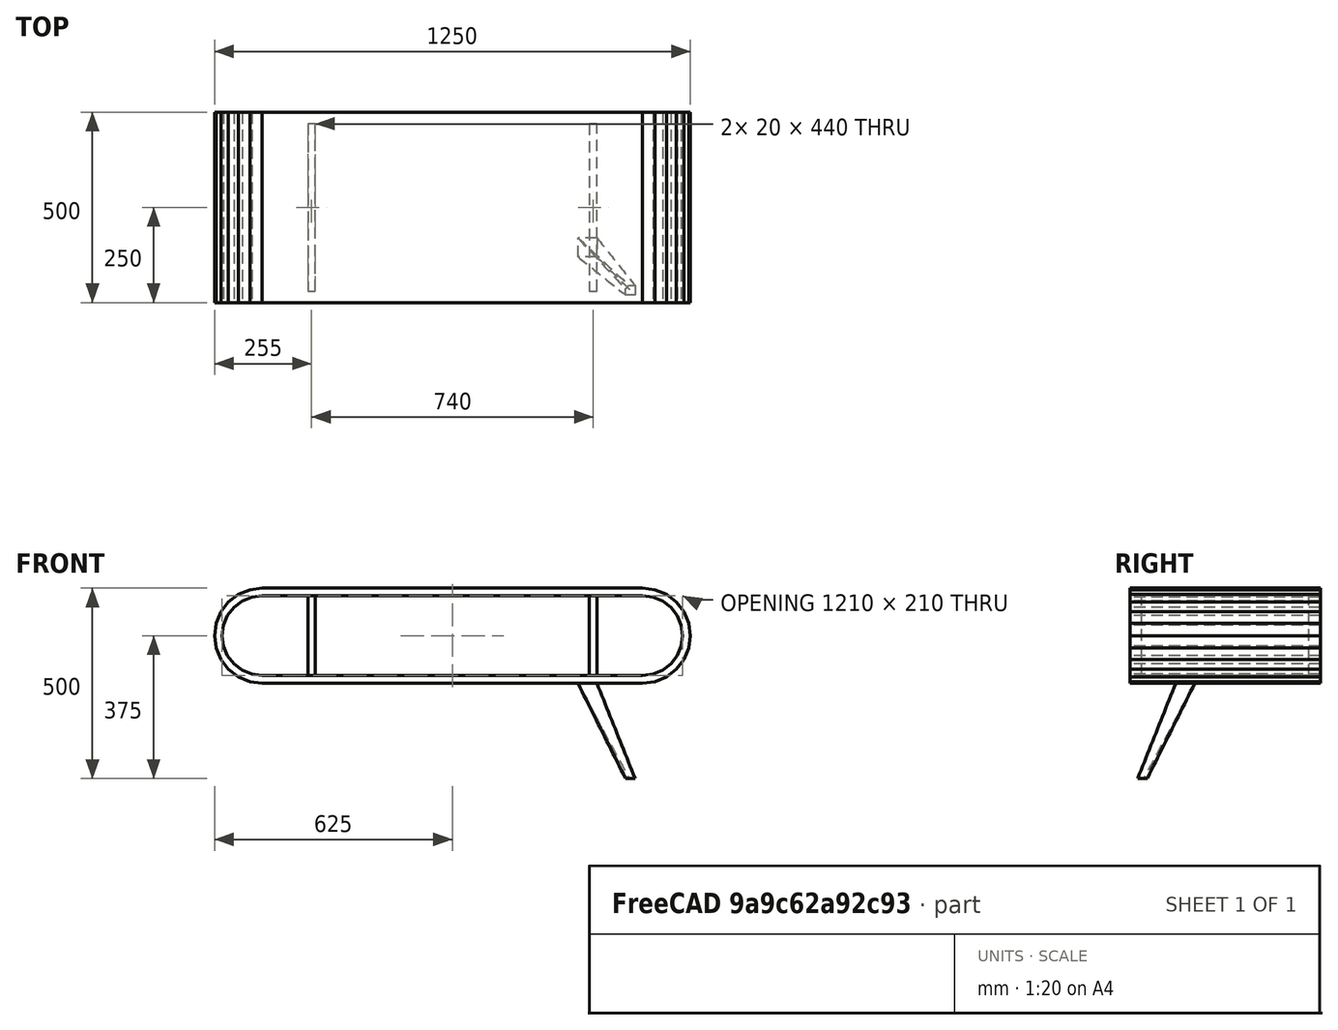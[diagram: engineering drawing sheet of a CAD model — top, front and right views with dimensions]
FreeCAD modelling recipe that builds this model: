
FCSTD DOCUMENT  (FreeCAD 0.22R35735 (Git))
Label: bendy
License: All rights reserved
LicenseURL: http://en.wikipedia.org/wiki/All_rights_reserved
objects: TechDraw::DrawViewDimension×14, Sketcher::SketchObject×4, PartDesign::Plane×4, Part::Mirroring×3, PartDesign::Pad×2, PartDesign::Body×2, TechDraw::DrawProjGroupItem×2, Spreadsheet::Sheet×1, PartDesign::AdditiveLoft×1, TechDraw::DrawSVGTemplate×1, TechDraw::DrawProjGroup×1, TechDraw::DrawPage×1
note: 41 computed .brp shape members not serialized (recipe doc carries the construction recipe); baked Part::Feature solids carry a one-line shape summary decoded from their .brp

FEATURE [Sketcher::SketchObject] Sketch
  FullyConstrained = true
  MapMode = 5
  Placement = pos=(0,0,0) rot=(1,0,0;1.5708rad)
  Support = -> [XZ_Plane]
  expr: Constraints[162] = Spreadsheet.thickness
  expr: Constraints[163] = Spreadsheet.thickness
  expr: Constraints[237] = Spreadsheet.total_height
  expr: Constraints[76] = Spreadsheet.total_length
  expr: Constraints[80] = Spreadsheet.top_height
  sketch-geometry (106):
    g0: LineSegment StartX=-4.97e-14 StartY=500 StartZ=0 EndX=1000 EndY=500 EndZ=0
    g1: LineSegment StartX=0 StartY=250 StartZ=0 EndX=1000 EndY=250 EndZ=0
    g2: LineSegment StartX=0 StartY=480 StartZ=0 EndX=1000 EndY=480 EndZ=0
    g3: LineSegment StartX=0 StartY=270 StartZ=0 EndX=1000 EndY=270 EndZ=0
    g4: LineSegment StartX=1105 StartY=375 StartZ=0 EndX=1101.42 EndY=402.176 EndZ=0
    g5: LineSegment StartX=1101.42 StartY=402.176 StartZ=0 EndX=1090.93 EndY=427.5 EndZ=0
    g6: LineSegment StartX=1090.93 StartY=427.5 StartZ=0 EndX=1074.25 EndY=449.246 EndZ=0
    g7: LineSegment StartX=1074.25 StartY=449.246 StartZ=0 EndX=1052.5 EndY=465.933 EndZ=0
    g8: LineSegment StartX=1052.5 StartY=465.933 StartZ=0 EndX=1027.18 EndY=476.422 EndZ=0
    g9: LineSegment StartX=1027.18 StartY=476.422 StartZ=0 EndX=1000 EndY=480 EndZ=0
    g10: LineSegment StartX=1000 StartY=480 StartZ=0 EndX=972.824 EndY=476.422 EndZ=0
    g11: LineSegment StartX=972.824 StartY=476.422 StartZ=0 EndX=947.5 EndY=465.933 EndZ=0
    g12: LineSegment StartX=947.5 StartY=465.933 StartZ=0 EndX=925.754 EndY=449.246 EndZ=0
    g13: LineSegment StartX=925.754 StartY=449.246 StartZ=0 EndX=909.067 EndY=427.5 EndZ=0
    g14: LineSegment StartX=909.067 StartY=427.5 StartZ=0 EndX=898.578 EndY=402.176 EndZ=0
    g15: LineSegment StartX=898.578 StartY=402.176 StartZ=0 EndX=895 EndY=375 EndZ=0
    g16: LineSegment StartX=895 StartY=375 StartZ=0 EndX=898.578 EndY=347.824 EndZ=0
    g17: LineSegment StartX=898.578 StartY=347.824 StartZ=0 EndX=909.067 EndY=322.5 EndZ=0
    g18: LineSegment StartX=909.067 StartY=322.5 StartZ=0 EndX=925.754 EndY=300.754 EndZ=0
    g19: LineSegment StartX=925.754 StartY=300.754 StartZ=0 EndX=947.5 EndY=284.067 EndZ=0
    g20: LineSegment StartX=947.5 StartY=284.067 StartZ=0 EndX=972.824 EndY=273.578 EndZ=0
    g21: LineSegment StartX=972.824 StartY=273.578 StartZ=0 EndX=1000 EndY=270 EndZ=0
    g22: LineSegment StartX=1000 StartY=270 StartZ=0 EndX=1027.18 EndY=273.578 EndZ=0
    g23: LineSegment StartX=1027.18 StartY=273.578 StartZ=0 EndX=1052.5 EndY=284.067 EndZ=0
    g24: LineSegment StartX=1052.5 StartY=284.067 StartZ=0 EndX=1074.25 EndY=300.754 EndZ=0
    g25: LineSegment StartX=1074.25 StartY=300.754 StartZ=0 EndX=1090.93 EndY=322.5 EndZ=0
    g26: LineSegment StartX=1090.93 StartY=322.5 StartZ=0 EndX=1101.42 EndY=347.824 EndZ=0
    g27: LineSegment StartX=1101.42 StartY=347.824 StartZ=0 EndX=1105 EndY=375 EndZ=0
    g28: Circle CenterX=1000 CenterY=375 CenterZ=0 NormalX=0 NormalY=0 NormalZ=1 AngleXU=0 Radius=105
    g29: LineSegment StartX=0 StartY=480 StartZ=0 EndX=-27.176 EndY=476.422 EndZ=0
    g30: LineSegment StartX=-27.176 StartY=476.422 StartZ=0 EndX=-52.5 EndY=465.933 EndZ=0
    g31: LineSegment StartX=-52.5 StartY=465.933 StartZ=0 EndX=-74.2462 EndY=449.246 EndZ=0
    g32: LineSegment StartX=-74.2462 StartY=449.246 StartZ=0 EndX=-90.9327 EndY=427.5 EndZ=0
    g33: LineSegment StartX=-90.9327 StartY=427.5 StartZ=0 EndX=-101.422 EndY=402.176 EndZ=0
    g34: LineSegment StartX=-101.422 StartY=402.176 StartZ=0 EndX=-105 EndY=375 EndZ=0
    g35: LineSegment StartX=-105 StartY=375 StartZ=0 EndX=-101.422 EndY=347.824 EndZ=0
    g36: LineSegment StartX=-101.422 StartY=347.824 StartZ=0 EndX=-90.9327 EndY=322.5 EndZ=0
    g37: LineSegment StartX=-90.9327 StartY=322.5 StartZ=0 EndX=-74.2462 EndY=300.754 EndZ=0
    g38: LineSegment StartX=-74.2462 StartY=300.754 StartZ=0 EndX=-52.5 EndY=284.067 EndZ=0
    g39: LineSegment StartX=-52.5 StartY=284.067 StartZ=0 EndX=-27.176 EndY=273.578 EndZ=0
    g40: LineSegment StartX=-27.176 StartY=273.578 StartZ=0 EndX=-7.1e-15 EndY=270 EndZ=0
    g41: LineSegment StartX=-7.1e-15 StartY=270 StartZ=0 EndX=27.176 EndY=273.578 EndZ=0
    g42: LineSegment StartX=27.176 StartY=273.578 StartZ=0 EndX=52.5 EndY=284.067 EndZ=0
    g43: LineSegment StartX=52.5 StartY=284.067 StartZ=0 EndX=74.2462 EndY=300.754 EndZ=0
    g44: LineSegment StartX=74.2462 StartY=300.754 StartZ=0 EndX=90.9327 EndY=322.5 EndZ=0
    g45: LineSegment StartX=90.9327 StartY=322.5 StartZ=0 EndX=101.422 EndY=347.824 EndZ=0
    g46: LineSegment StartX=101.422 StartY=347.824 StartZ=0 EndX=105 EndY=375 EndZ=0
    g47: LineSegment StartX=105 StartY=375 StartZ=0 EndX=101.422 EndY=402.176 EndZ=0
    g48: LineSegment StartX=101.422 StartY=402.176 StartZ=0 EndX=90.9327 EndY=427.5 EndZ=0
    g49: LineSegment StartX=90.9327 StartY=427.5 StartZ=0 EndX=74.2462 EndY=449.246 EndZ=0
    g50: LineSegment StartX=74.2462 StartY=449.246 StartZ=0 EndX=52.5 EndY=465.933 EndZ=0
    g51: LineSegment StartX=52.5 StartY=465.933 StartZ=0 EndX=27.176 EndY=476.422 EndZ=0
    g52: LineSegment StartX=27.176 StartY=476.422 StartZ=0 EndX=0 EndY=480 EndZ=0
    g53: Circle CenterX=0 CenterY=375 CenterZ=0 NormalX=0 NormalY=0 NormalZ=1 AngleXU=0 Radius=105
    g54: LineSegment StartX=0 StartY=480 StartZ=0 EndX=0 EndY=375 EndZ=0
    g55: LineSegment StartX=0 StartY=375 StartZ=0 EndX=0 EndY=270 EndZ=0
    g56: LineSegment StartX=-4.97e-14 StartY=500 StartZ=0 EndX=-32.3524 EndY=495.741 EndZ=0
    g57: LineSegment StartX=-32.3524 StartY=495.741 StartZ=0 EndX=-62.5 EndY=483.253 EndZ=0
    g58: LineSegment StartX=-62.5 StartY=483.253 StartZ=0 EndX=-88.3883 EndY=463.388 EndZ=0
    g59: LineSegment StartX=-88.3883 StartY=463.388 StartZ=0 EndX=-108.253 EndY=437.5 EndZ=0
    g60: LineSegment StartX=-108.253 StartY=437.5 StartZ=0 EndX=-120.741 EndY=407.352 EndZ=0
    g61: LineSegment StartX=-120.741 StartY=407.352 StartZ=0 EndX=-125 EndY=375 EndZ=0
    g62: LineSegment StartX=-125 StartY=375 StartZ=0 EndX=-120.741 EndY=342.648 EndZ=0
    g63: LineSegment StartX=-120.741 StartY=342.648 StartZ=0 EndX=-108.253 EndY=312.5 EndZ=0
    g64: LineSegment StartX=-108.253 StartY=312.5 StartZ=0 EndX=-88.3883 EndY=286.612 EndZ=0
    g65: LineSegment StartX=-88.3883 StartY=286.612 StartZ=0 EndX=-62.5 EndY=266.747 EndZ=0
    g66: LineSegment StartX=-62.5 StartY=266.747 StartZ=0 EndX=-32.3524 EndY=254.259 EndZ=0
    g67: LineSegment StartX=-32.3524 StartY=254.259 StartZ=0 EndX=4.97e-14 EndY=250 EndZ=0
    g68: LineSegment StartX=4.97e-14 StartY=250 StartZ=0 EndX=32.3524 EndY=254.259 EndZ=0
    g69: LineSegment StartX=32.3524 StartY=254.259 StartZ=0 EndX=62.5 EndY=266.747 EndZ=0
    g70: LineSegment StartX=62.5 StartY=266.747 StartZ=0 EndX=88.3883 EndY=286.612 EndZ=0
    g71: LineSegment StartX=88.3883 StartY=286.612 StartZ=0 EndX=108.253 EndY=312.5 EndZ=0
    g72: LineSegment StartX=108.253 StartY=312.5 StartZ=0 EndX=120.741 EndY=342.648 EndZ=0
    g73: LineSegment StartX=120.741 StartY=342.648 StartZ=0 EndX=125 EndY=375 EndZ=0
    g74: LineSegment StartX=125 StartY=375 StartZ=0 EndX=120.741 EndY=407.352 EndZ=0
    g75: LineSegment StartX=120.741 StartY=407.352 StartZ=0 EndX=108.253 EndY=437.5 EndZ=0
    g76: LineSegment StartX=108.253 StartY=437.5 StartZ=0 EndX=88.3883 EndY=463.388 EndZ=0
    g77: LineSegment StartX=88.3883 StartY=463.388 StartZ=0 EndX=62.5 EndY=483.253 EndZ=0
    g78: LineSegment StartX=62.5 StartY=483.253 StartZ=0 EndX=32.3524 EndY=495.741 EndZ=0
    g79: LineSegment StartX=32.3524 StartY=495.741 StartZ=0 EndX=-4.97e-14 EndY=500 EndZ=0
    g80: Circle CenterX=0 CenterY=375 CenterZ=0 NormalX=0 NormalY=0 NormalZ=1 AngleXU=0 Radius=125
    g81: LineSegment StartX=1000 StartY=500 StartZ=0 EndX=967.648 EndY=495.741 EndZ=0
    g82: LineSegment StartX=967.648 StartY=495.741 StartZ=0 EndX=937.5 EndY=483.253 EndZ=0
    g83: LineSegment StartX=937.5 StartY=483.253 StartZ=0 EndX=911.612 EndY=463.388 EndZ=0
    g84: LineSegment StartX=911.612 StartY=463.388 StartZ=0 EndX=891.747 EndY=437.5 EndZ=0
    g85: LineSegment StartX=891.747 StartY=437.5 StartZ=0 EndX=879.259 EndY=407.352 EndZ=0
    g86: LineSegment StartX=879.259 StartY=407.352 StartZ=0 EndX=875 EndY=375 EndZ=0
    g87: LineSegment StartX=875 StartY=375 StartZ=0 EndX=879.259 EndY=342.648 EndZ=0
    g88: LineSegment StartX=879.259 StartY=342.648 StartZ=0 EndX=891.747 EndY=312.5 EndZ=0
    g89: LineSegment StartX=891.747 StartY=312.5 StartZ=0 EndX=911.612 EndY=286.612 EndZ=0
    g90: LineSegment StartX=911.612 StartY=286.612 StartZ=0 EndX=937.5 EndY=266.747 EndZ=0
    g91: LineSegment StartX=937.5 StartY=266.747 StartZ=0 EndX=967.648 EndY=254.259 EndZ=0
    g92: LineSegment StartX=967.648 StartY=254.259 StartZ=0 EndX=1000 EndY=250 EndZ=0
    g93: LineSegment StartX=1000 StartY=250 StartZ=0 EndX=1032.35 EndY=254.259 EndZ=0
    g94: LineSegment StartX=1032.35 StartY=254.259 StartZ=0 EndX=1062.5 EndY=266.747 EndZ=0
    g95: LineSegment StartX=1062.5 StartY=266.747 StartZ=0 EndX=1088.39 EndY=286.612 EndZ=0
    g96: LineSegment StartX=1088.39 StartY=286.612 StartZ=0 EndX=1108.25 EndY=312.5 EndZ=0
    g97: LineSegment StartX=1108.25 StartY=312.5 StartZ=0 EndX=1120.74 EndY=342.648 EndZ=0
    g98: LineSegment StartX=1120.74 StartY=342.648 StartZ=0 EndX=1125 EndY=375 EndZ=0
    g99: LineSegment StartX=1125 StartY=375 StartZ=0 EndX=1120.74 EndY=407.352 EndZ=0
    g100: LineSegment StartX=1120.74 StartY=407.352 StartZ=0 EndX=1108.25 EndY=437.5 EndZ=0
    g101: LineSegment StartX=1108.25 StartY=437.5 StartZ=0 EndX=1088.39 EndY=463.388 EndZ=0
    g102: LineSegment StartX=1088.39 StartY=463.388 StartZ=0 EndX=1062.5 EndY=483.253 EndZ=0
    g103: LineSegment StartX=1062.5 StartY=483.253 StartZ=0 EndX=1032.35 EndY=495.741 EndZ=0
    g104: LineSegment StartX=1032.35 StartY=495.741 StartZ=0 EndX=1000 EndY=500 EndZ=0
    g105: Circle CenterX=1000 CenterY=375 CenterZ=0 NormalX=0 NormalY=0 NormalZ=1 AngleXU=0 Radius=125
  constraints (226):
    c: Horizontal(g0)
    c: Horizontal(g2)
    c: Coincident(g4,g5)
    c: Coincident(g5,g6)
    c: Coincident(g6,g7)
    c: Coincident(g7,g8)
    c: Coincident(g8,g9)
    c: Coincident(g9,g10)
    c: Coincident(g10,g11)
    c: Coincident(g11,g12)
    c: Coincident(g12,g13)
    c: Coincident(g13,g14)
    c: Coincident(g14,g15)
    c: Coincident(g15,g16)
    c: Coincident(g16,g17)
    c: Coincident(g17,g18)
    c: Coincident(g18,g19)
    c: Coincident(g19,g20)
    c: Coincident(g20,g21)
    c: Coincident(g21,g22)
    c: Coincident(g22,g23)
    c: Coincident(g23,g24)
    c: Coincident(g24,g25)
    c: Coincident(g25,g26)
    c: Coincident(g26,g27)
    c: Coincident(g27,g4)
    c: Equal(g4, g5-g27) x23
    c: PointOnObject(g4,g28)
    c: PointOnObject(g5,g28)
    c: PointOnObject(g6,g28)
    c: PointOnObject(g7,g28)
    c: PointOnObject(g8,g28)
    c: PointOnObject(g9,g28)
    c: PointOnObject(g10,g28)
    c: PointOnObject(g11,g28)
    c: PointOnObject(g12,g28)
    c: PointOnObject(g13,g28)
    c: PointOnObject(g14,g28)
    c: PointOnObject(g15,g28)
    c: PointOnObject(g16,g28)
    c: PointOnObject(g17,g28)
    c: PointOnObject(g18,g28)
    c: PointOnObject(g19,g28)
    c: PointOnObject(g20,g28)
    c: PointOnObject(g21,g28)
    c: PointOnObject(g22,g28)
    c: PointOnObject(g23,g28)
    c: PointOnObject(g24,g28)
    c: PointOnObject(g25,g28)
    c: PointOnObject(g26,g28)
    c: PointOnObject(g27,g28)
    c: Equal(g0,g2)
    c: Equal(g2,g3)
    c: Equal(g3,g1)
    c: DistanceX(g0,g0) = 1000
    c: Vertical(g28,g2)
    c: Horizontal(g1)
    c: Horizontal(g3)
    c: DistanceY(g1,g0) = 250
    c: Coincident(g9,g2)
    c: Coincident(g29,g30)
    c: Coincident(g30,g31)
    c: Coincident(g31,g32)
    c: Coincident(g32,g33)
    c: Coincident(g33,g34)
    c: Coincident(g34,g35)
    c: Coincident(g35,g36)
    c: Coincident(g36,g37)
    c: Coincident(g37,g38)
    c: Coincident(g38,g39)
    c: Coincident(g39,g40)
    c: Coincident(g40,g41)
    c: Coincident(g41,g42)
    c: Coincident(g42,g43)
    c: Coincident(g43,g44)
    c: Coincident(g44,g45)
    c: Coincident(g45,g46)
    c: Coincident(g46,g47)
    c: Coincident(g47,g48)
    c: Coincident(g48,g49)
    c: Coincident(g49,g50)
    c: Coincident(g50,g51)
    c: Coincident(g51,g52)
    c: Coincident(g52,g29)
    c: Equal(g29, g30-g52) x23
    c: PointOnObject(g29,g53)
    c: PointOnObject(g30,g53)
    c: PointOnObject(g31,g53)
    c: PointOnObject(g32,g53)
    c: PointOnObject(g33,g53)
    c: PointOnObject(g34,g53)
    c: PointOnObject(g35,g53)
    c: PointOnObject(g36,g53)
    c: PointOnObject(g37,g53)
    c: PointOnObject(g38,g53)
    c: PointOnObject(g39,g53)
    c: PointOnObject(g40,g53)
    c: PointOnObject(g41,g53)
    c: PointOnObject(g42,g53)
    c: PointOnObject(g43,g53)
    c: PointOnObject(g44,g53)
    c: PointOnObject(g45,g53)
    c: PointOnObject(g46,g53)
    c: PointOnObject(g47,g53)
    c: PointOnObject(g48,g53)
    c: PointOnObject(g49,g53)
    c: PointOnObject(g50,g53)
    c: PointOnObject(g51,g53)
    c: PointOnObject(g52,g53)
    c: PointOnObject(g53,g-2)
    c: Coincident(g52,g2)
    c: Coincident(g54,g2)
    c: Coincident(g54,g53)
    c: Vertical(g54)
    c: Coincident(g55,g53)
    c: Coincident(g55,g3)
    c: Vertical(g55)
    c: Equal(g54,g55)
    c: DistanceY(g1,g3) = 20
    c: DistanceY(g2,g0) = 20
    c: Coincident(g56,g57)
    c: Coincident(g57,g58)
    c: Coincident(g58,g59)
    c: Coincident(g59,g60)
    c: Coincident(g60,g61)
    c: Coincident(g61,g62)
    c: Coincident(g62,g63)
    c: Coincident(g63,g64)
    c: Coincident(g64,g65)
    c: Coincident(g65,g66)
    c: Coincident(g66,g67)
    c: Coincident(g67,g68)
    c: Coincident(g68,g69)
    c: Coincident(g69,g70)
    c: Coincident(g70,g71)
    c: Coincident(g71,g72)
    c: Coincident(g72,g73)
    c: Coincident(g73,g74)
    c: Coincident(g74,g75)
    c: Coincident(g75,g76)
    c: Coincident(g76,g77)
    c: Coincident(g77,g78)
    c: Coincident(g78,g79)
    c: Coincident(g79,g56)
    c: Equal(g56, g57-g79) x23
    c: PointOnObject(g56,g80)
    c: PointOnObject(g57,g80)
    c: PointOnObject(g58,g80)
    c: PointOnObject(g59,g80)
    c: PointOnObject(g60,g80)
    c: PointOnObject(g61,g80)
    c: PointOnObject(g62,g80)
    c: PointOnObject(g63,g80)
    c: PointOnObject(g64,g80)
    c: PointOnObject(g65,g80)
    c: PointOnObject(g66,g80)
    c: PointOnObject(g67,g80)
    c: PointOnObject(g68,g80)
    c: PointOnObject(g69,g80)
    c: PointOnObject(g70,g80)
    c: PointOnObject(g71,g80)
    c: PointOnObject(g72,g80)
    c: PointOnObject(g73,g80)
    c: PointOnObject(g74,g80)
    c: PointOnObject(g75,g80)
    c: PointOnObject(g76,g80)
    c: PointOnObject(g77,g80)
    c: PointOnObject(g78,g80)
    c: PointOnObject(g79,g80)
    c: Horizontal(g28,g53)
    c: Coincident(g80,g53)
    c: DistanceY(g-1,g0) = 500
    c: Coincident(g0,g56)
    c: Vertical(g3,g1)
    c: Coincident(g81,g82)
    c: Coincident(g82,g83)
    c: Coincident(g83,g84)
    c: Coincident(g84,g85)
    c: Coincident(g85,g86)
    c: Coincident(g86,g87)
    c: Coincident(g87,g88)
    c: Coincident(g88,g89)
    c: Coincident(g89,g90)
    c: Coincident(g90,g91)
    c: Coincident(g91,g92)
    c: Coincident(g92,g93)
    c: Coincident(g93,g94)
    c: Coincident(g94,g95)
    c: Coincident(g95,g96)
    c: Coincident(g96,g97)
    c: Coincident(g97,g98)
    c: Coincident(g98,g99)
    c: Coincident(g99,g100)
    c: Coincident(g100,g101)
    c: Coincident(g101,g102)
    c: Coincident(g102,g103)
    c: Coincident(g103,g104)
    c: Coincident(g104,g81)
    c: Equal(g81, g82-g104) x23
    c: PointOnObject(g81,g105)
    c: PointOnObject(g82,g105)
    c: PointOnObject(g83,g105)
    c: PointOnObject(g84,g105)
    c: PointOnObject(g85,g105)
    c: PointOnObject(g86,g105)
    c: PointOnObject(g87,g105)
    c: PointOnObject(g88,g105)
    c: PointOnObject(g89,g105)
    c: PointOnObject(g90,g105)
    c: PointOnObject(g91,g105)
    c: PointOnObject(g92,g105)
    c: PointOnObject(g93,g105)
    c: PointOnObject(g94,g105)
    c: PointOnObject(g95,g105)
    c: PointOnObject(g96,g105)
    c: PointOnObject(g97,g105)
    c: PointOnObject(g98,g105)
    c: PointOnObject(g99,g105)
    c: PointOnObject(g100,g105)
    c: PointOnObject(g101,g105)
    c: PointOnObject(g102,g105)
    c: PointOnObject(g103,g105)
    c: PointOnObject(g104,g105)
    c: Coincident(g105,g28)
    c: Coincident(g104,g0)
    c: PointOnObject(g0,g-2)
FEATURE [Spreadsheet::Sheet] Spreadsheet
  cells = A1='Total Length; B1(total_length)=1000; A2='Depth; B2(depth)=500; A3='Thickness; B3(thickness)=20; A4='total height; B4(total_height)=500; A5='top part height; B5(top_height)=250
FEATURE [PartDesign::Pad] Pad
  Direction = (0,-1,2e-16)
  Length = 500
  Length2 = 10
  Placement = pos=(0,0,0) rot=(1,0,0;1.5708rad)
  Profile = -> Sketch
  ReferenceAxis = -> Sketch [N_Axis]
  Type = 0
  expr: Length = Spreadsheet.depth
FEATURE [PartDesign::Plane] DatumPlane
  AttachmentOffset = pos=(0,0,250) rot=(0,0,1;0rad)
  Length = 60
  MapMode = 5
  Placement = pos=(0,0,250) rot=(0,0,1;0rad)
  ResizeMode = 0
  Support = -> [XY_Plane001]
  Width = 60
  expr: .AttachmentOffset.Base.z = Spreadsheet.total_height - Spreadsheet.top_height
FEATURE [Sketcher::SketchObject] Sketch001  label="TopSk"
  FullyConstrained = true
  MapMode = 5
  Placement = pos=(0,0,250) rot=(0,0,1;0rad)
  Support = -> [DatumPlane]
  expr: Constraints[11] = Spreadsheet.depth - 120
  sketch-geometry (5):
    g0: LineSegment StartX=120 StartY=-380 StartZ=0 EndX=170 EndY=-380 EndZ=0
    g1: LineSegment StartX=120 StartY=-330 StartZ=0 EndX=120 EndY=-380 EndZ=0
    g2: LineSegment StartX=170 StartY=-380 StartZ=0 EndX=170 EndY=-330.071 EndZ=0
    g3: LineSegment StartX=120 StartY=-330 StartZ=0 EndX=169.929 EndY=-330 EndZ=0
    g4: LineSegment StartX=169.929 StartY=-330 StartZ=0 EndX=170 EndY=-330.071 EndZ=0
  constraints (15):
    c: Coincident(g0,g2)
    c: Coincident(g1,g0)
    c: Horizontal(g0)
    c: Vertical(g1)
    c: DistanceX(g-1,g0) = 120
    c: Vertical(g2)
    c: Coincident(g3,g1)
    c: Horizontal(g3)
    c: Equal(g2,g3)
    c: Coincident(g4,g3)
    c: Coincident(g4,g2)
    c: DistanceY(g0,g-1) = 380
    c: Equal(g1,g0)
    c: DistanceY(g1,g1) = 50
    c: Distance(g4) = 0.1
FEATURE [Sketcher::SketchObject] Sketch002  label="BottomSk"
  ExternalGeometry = -> [Sketch001]
  FullyConstrained = false
  MapMode = 5
  Support = -> [XY_Plane001]
  sketch-geometry (9):
    g0: LineSegment StartX=20 StartY=-455 StartZ=0 EndX=20 EndY=-480 EndZ=0
    g1: LineSegment StartX=20 StartY=-480 StartZ=0 EndX=45 EndY=-480 EndZ=0
    g2: LineSegment StartX=45 StartY=-480 StartZ=0 EndX=45 EndY=-464.27 EndZ=0
    g3: LineSegment StartX=35.7297 StartY=-455 StartZ=0 EndX=20 EndY=-455 EndZ=0
    g4: LineSegment StartX=120 StartY=-380 StartZ=0 EndX=20 EndY=-380 EndZ=0
    g5: LineSegment StartX=20 StartY=-380 StartZ=0 EndX=20 EndY=-480 EndZ=0
    g6: LineSegment StartX=20 StartY=-480 StartZ=0 EndX=120 EndY=-480 EndZ=0
    g7: LineSegment StartX=120 StartY=-480 StartZ=0 EndX=120 EndY=-380 EndZ=0
    g8: LineSegment StartX=45 StartY=-464.27 StartZ=0 EndX=35.7297 EndY=-455 EndZ=0
  constraints (24):
    c: Coincident(g3,g0)
    c: Coincident(g0,g1)
    c: Coincident(g1,g2)
    c: Horizontal(g1)
    c: Vertical(g0)
    c: Vertical(g2)
    c: Coincident(g8,g3)
    c: Horizontal(g3)
    c: DistanceY(g0,g0) = 25
    c: Coincident(g4,g5)
    c: Coincident(g5,g6)
    c: Coincident(g6,g7)
    c: Coincident(g7,g4)
    c: Horizontal(g4)
    c: Horizontal(g6)
    c: Vertical(g5)
    c: Vertical(g7)
    c: Coincident(g4,g-4)
    c: Coincident(g5,g0)
    c: Equal(g6,g5)
    c: Angle(g8,g3) = 0.785398
    c: Coincident(g8,g2)
    c: DistanceX(g6,g6) = 100
    c: Equal(g0,g1)
FEATURE [PartDesign::AdditiveLoft] AdditiveLoft
  Closed = false
  Placement = pos=(0,0,250) rot=(0,0,1;0rad)
  Profile = -> Sketch001
  Ruled = false
  Sections = -> [Sketch002]
FEATURE [PartDesign::Plane] DatumPlane001
  AttachmentOffset = pos=(0,0,250) rot=(0,0,1;0rad)
  Length = 60
  MapMode = 5
  Placement = pos=(0,-250,5.55e-14) rot=(1,0,0;1.5708rad)
  ResizeMode = 0
  Support = -> [XZ_Plane001]
  Width = 60
  expr: .AttachmentOffset.Base.z = Spreadsheet.depth / 2
FEATURE [PartDesign::Plane] DatumPlane002
  AttachmentOffset = pos=(0,0,500) rot=(0,0,1;0rad)
  Length = 60
  MapMode = 5
  Placement = pos=(500,0,0) rot=(0.57735,0.57735,0.57735;2.0944rad)
  ResizeMode = 0
  Support = -> [YZ_Plane001]
  Width = 60
  expr: .AttachmentOffset.Base.z = Spreadsheet.total_length / 2
FEATURE [PartDesign::Body] Body001  label="Leg"
  Group = -> [DatumPlane,Sketch001,Sketch002,AdditiveLoft,DatumPlane001,DatumPlane002]
  Origin = -> Origin001
  Tip = -> AdditiveLoft
FEATURE [Part::Mirroring] Part__Mirroring  label="Leg2"
  Base = (0,-250,5.55e-14)
  MirrorPlane = -> DatumPlane001 [Plane]
  Normal = (0,-1,2e-16)
  Source = -> Body001
FEATURE [Part::Mirroring] Part__Mirroring001  label="Leg3"
  Base = (500,0,0)
  MirrorPlane = -> DatumPlane002 [Plane]
  Normal = (1,0,0)
  Source = -> Part__Mirroring
FEATURE [Part::Mirroring] Part__Mirroring002  label="Leg4"
  Base = (0,-250,5.55e-14)
  MirrorPlane = -> DatumPlane001
  Normal = (0,-1,2e-16)
  Source = -> Part__Mirroring001
FEATURE [TechDraw::DrawSVGTemplate] Template
  Height = 215.9
  Orientation = 1
  Template = <path>
  Width = 279.4
FEATURE [PartDesign::Plane] DatumPlane003
  AttachmentOffset = pos=(0,0,270) rot=(0,0,1;0rad)
  Length = 60
  MapMode = 5
  Placement = pos=(0,0,270) rot=(0,0,1;0rad)
  ResizeMode = 0
  Support = -> [XY_Plane]
  Width = 60
  expr: .AttachmentOffset.Base.z = Spreadsheet.total_height - Spreadsheet.top_height + Spreadsheet.thickness
FEATURE [Sketcher::SketchObject] Sketch003
  ExternalGeometry = -> [Sketch]
  FullyConstrained = false
  MapMode = 5
  Placement = pos=(0,0,270) rot=(0,0,1;0rad)
  Support = -> [DatumPlane003]
  expr: Constraints[15] = Spreadsheet.thickness
  expr: Constraints[17] = Spreadsheet.thickness
  expr: Constraints[20] = Spreadsheet.depth / 2
  sketch-geometry (9):
    g0: LineSegment StartX=120 StartY=-30 StartZ=0 EndX=120 EndY=-470 EndZ=0
    g1: LineSegment StartX=120 StartY=-470 StartZ=0 EndX=140 EndY=-470 EndZ=0
    g2: LineSegment StartX=140 StartY=-470 StartZ=0 EndX=140 EndY=-30 EndZ=0
    g3: LineSegment StartX=140 StartY=-30 StartZ=0 EndX=120 EndY=-30 EndZ=0
    g4: LineSegment StartX=860 StartY=-30 StartZ=0 EndX=860 EndY=-470 EndZ=0
    g5: LineSegment StartX=860 StartY=-470 StartZ=0 EndX=880 EndY=-470 EndZ=0
    g6: LineSegment StartX=880 StartY=-470 StartZ=0 EndX=880 EndY=-30 EndZ=0
    g7: LineSegment StartX=880 StartY=-30 StartZ=0 EndX=860 EndY=-30 EndZ=0
    g8: LineSegment StartX=0 StartY=-250 StartZ=0 EndX=1101.7 EndY=-250 EndZ=0
  constraints (26):
    c: Coincident(g0,g1)
    c: Coincident(g1,g2)
    c: Coincident(g2,g3)
    c: Coincident(g3,g0)
    c: Horizontal(g1)
    c: Horizontal(g3)
    c: Coincident(g4,g5)
    c: Coincident(g5,g6)
    c: Coincident(g6,g7)
    c: Coincident(g7,g4)
    c: Vertical(g4)
    c: Vertical(g6)
    c: Horizontal(g5)
    c: Horizontal(g7)
    c: DistanceX(g-1,g0) = 120
    c: DistanceX(g0,g2) = 20
    c: DistanceX(g6,g-4) = 120
    c: DistanceX(g4,g6) = 20
    c: PointOnObject(g8,g-2)
    c: Horizontal(g8)
    c: DistanceY(g8,g-4) = 250
    c: Symmetric(g0,g0,g8)
    c: Equal(g2,g4)
    c: DistanceY(g0,g-1) = 30
    c: Parallel(g2,g0)
    c: Horizontal(g4,g2)
FEATURE [PartDesign::Pad] Pad001
  BaseFeature = -> Pad
  Direction = (0,0,1)
  Length = 210
  Length2 = 10
  Placement = pos=(0,0,0) rot=(1,0,0;1.5708rad)
  Profile = -> Sketch003
  ReferenceAxis = -> Sketch003 [N_Axis]
  Type = 0
  expr: Length = Spreadsheet.top_height - 2 * Spreadsheet.thickness
FEATURE [PartDesign::Body] Body  label="Top"
  Group = -> [Sketch,Pad,DatumPlane003,Sketch003,Pad001]
  Origin = -> Origin
  Tip = -> Pad001
FEATURE [TechDraw::DrawProjGroupItem] ProjItem  label="Front"
  CoarseView = false
  Direction = (0,-1,0)
  Focus = 100
  HardHidden = false
  IsoCount = 0
  IsoHidden = false
  IsoVisible = false
  LockPosition = true
  Perspective = false
  Rotation = 0
  RotationVector = (1,0,0)
  Scale = 0.166667
  ScaleType = 2
  ScrubCount = 0
  SeamHidden = false
  SeamVisible = false
  SmoothHidden = false
  SmoothVisible = true
  Source = -> [Part__Mirroring002,Part__Mirroring001,Part__Mirroring,Body001,Pad001]
  Type = 0
  X = 0
  XDirection = (1,0,0)
  Y = 0
FEATURE [TechDraw::DrawProjGroupItem] ProjItem002  label="Bottom"
  CoarseView = false
  Direction = (0,0,-1)
  Focus = 100
  HardHidden = false
  IsoCount = 0
  IsoHidden = false
  IsoVisible = false
  LockPosition = false
  Perspective = false
  Rotation = 0
  RotationVector = (1,0,0)
  Scale = 0.166667
  ScaleType = 2
  ScrubCount = 0
  SeamHidden = false
  SeamVisible = false
  SmoothHidden = false
  SmoothVisible = true
  Source = -> [Part__Mirroring002,Part__Mirroring001,Part__Mirroring,Body001,Pad001]
  Type = 5
  X = 0
  XDirection = (1,0,0)
  Y = 98.3335
FEATURE [TechDraw::DrawProjGroup] ProjGroup
  Anchor = -> ProjItem
  AutoDistribute = true
  LockPosition = false
  ProjectionType = 0
  Rotation = 0
  Scale = 0.166667
  ScaleType = 2
  Source = -> [Part__Mirroring002,Part__Mirroring001,Part__Mirroring,Body001,Pad001]
  Views = -> [ProjItem,ProjItem002]
  X = 140.254
  Y = 59.7927
  spacingX = 15
  spacingY = 15
FEATURE [TechDraw::DrawViewDimension] Dimension003
  AngleOverride = false
  Arbitrary = false
  ArbitraryTolerances = false
  EqualTolerance = true
  ExtensionAngle = 0
  FormatSpec = %.0w
  FormatSpecOverTolerance = %+.0w
  FormatSpecUnderTolerance = %+.0w
  Inverted = false
  LineAngle = 0
  LockPosition = false
  MeasureType = 1
  OverTolerance = 0
  References2D = -> [ProjItem002]
  Rotation = 0
  ScaleType = 0
  TheoreticalExact = false
  Type = 2
  UnderTolerance = 0
  X = -46.8584
  Y = -29.7494
FEATURE [TechDraw::DrawViewDimension] Dimension005
  AngleOverride = false
  Arbitrary = false
  ArbitraryTolerances = false
  EqualTolerance = true
  ExtensionAngle = 0
  FormatSpec = %.0w
  FormatSpecOverTolerance = %+.0w
  FormatSpecUnderTolerance = %+.0w
  Inverted = false
  LineAngle = 0
  LockPosition = false
  MeasureType = 1
  OverTolerance = 0
  References2D = -> [ProjItem002]
  Rotation = 0
  ScaleType = 0
  TheoreticalExact = false
  Type = 1
  UnderTolerance = 0
  X = -59.5731
  Y = -7.54534
FEATURE [TechDraw::DrawViewDimension] Dimension006
  AngleOverride = false
  Arbitrary = false
  ArbitraryTolerances = false
  EqualTolerance = true
  ExtensionAngle = 0
  FormatSpec = %.0w
  FormatSpecOverTolerance = %+.0w
  FormatSpecUnderTolerance = %+.0w
  Inverted = false
  LineAngle = 0
  LockPosition = false
  MeasureType = 1
  OverTolerance = 0
  References2D = -> [ProjItem002]
  Rotation = 0
  ScaleType = 0
  TheoreticalExact = false
  Type = 2
  UnderTolerance = 0
  X = -52.1972
  Y = -16.2559
FEATURE [TechDraw::DrawViewDimension] Dimension008
  AngleOverride = false
  Arbitrary = false
  ArbitraryTolerances = false
  EqualTolerance = true
  ExtensionAngle = 0
  FormatSpec = %.0w
  FormatSpecOverTolerance = %+.0w
  FormatSpecUnderTolerance = %+.0w
  Inverted = false
  LineAngle = 0
  LockPosition = false
  MeasureType = 1
  OverTolerance = 0
  References2D = -> [ProjItem]
  Rotation = 0
  ScaleType = 0
  TheoreticalExact = false
  Type = 0
  UnderTolerance = 0
  X = -79.0077
  Y = -14.7493
FEATURE [TechDraw::DrawViewDimension] Dimension009
  AngleOverride = false
  Arbitrary = false
  ArbitraryTolerances = false
  EqualTolerance = true
  ExtensionAngle = 0
  FormatSpec = %.0w
  FormatSpecOverTolerance = %+.0w
  FormatSpecUnderTolerance = %+.0w
  Inverted = false
  LineAngle = 0
  LockPosition = false
  MeasureType = 1
  OverTolerance = 0
  References2D = -> [ProjItem]
  Rotation = 0
  ScaleType = 0
  TheoreticalExact = false
  Type = 0
  UnderTolerance = 0
  X = -61.9465
  Y = -17.2853
FEATURE [TechDraw::DrawViewDimension] Dimension
  AngleOverride = false
  Arbitrary = false
  ArbitraryTolerances = false
  EqualTolerance = true
  ExtensionAngle = 0
  FormatSpec = %.0w
  FormatSpecOverTolerance = %+.0w
  FormatSpecUnderTolerance = %+.0w
  Inverted = false
  LineAngle = 0
  LockPosition = false
  MeasureType = 1
  OverTolerance = 0
  References2D = -> [ProjItem]
  Rotation = 0
  ScaleType = 0
  TheoreticalExact = false
  Type = 2
  UnderTolerance = 0
  X = 116.863
  Y = -2.86191
FEATURE [TechDraw::DrawViewDimension] Dimension010
  AngleOverride = false
  Arbitrary = false
  ArbitraryTolerances = false
  EqualTolerance = true
  ExtensionAngle = 0
  FormatSpec = %.0w
  FormatSpecOverTolerance = %+.0w
  FormatSpecUnderTolerance = %+.0w
  Inverted = false
  LineAngle = 0
  LockPosition = false
  MeasureType = 1
  OverTolerance = 0
  References2D = -> [ProjItem]
  Rotation = 0
  ScaleType = 0
  TheoreticalExact = false
  Type = 2
  UnderTolerance = 0
  X = 41.0378
  Y = -22.588
FEATURE [TechDraw::DrawViewDimension] Dimension016
  AngleOverride = false
  Arbitrary = false
  ArbitraryTolerances = false
  EqualTolerance = true
  ExtensionAngle = 0
  FormatSpec = %.0w
  FormatSpecOverTolerance = %+.0w
  FormatSpecUnderTolerance = %+.0w
  Inverted = false
  LineAngle = 0
  LockPosition = false
  MeasureType = 1
  OverTolerance = 0
  References2D = -> [ProjItem002]
  Rotation = 0
  ScaleType = 0
  TheoreticalExact = false
  Type = 1
  UnderTolerance = 0
  X = -77.8889
  Y = -20.9261
FEATURE [TechDraw::DrawViewDimension] Dimension020
  AngleOverride = false
  Arbitrary = false
  ArbitraryTolerances = false
  EqualTolerance = true
  ExtensionAngle = 0
  FormatSpec = %.1w
  FormatSpecOverTolerance = %+.0w
  FormatSpecUnderTolerance = %+.0w
  Inverted = false
  LineAngle = 0
  LockPosition = false
  MeasureType = 1
  OverTolerance = 0
  References2D = -> [ProjItem]
  Rotation = 0
  ScaleType = 0
  TheoreticalExact = false
  Type = 7
  UnderTolerance = 0
  X = -110.425
  Y = 37.4885
FEATURE [TechDraw::DrawViewDimension] Dimension021
  AngleOverride = false
  Arbitrary = false
  ArbitraryTolerances = false
  EqualTolerance = true
  ExtensionAngle = 0
  FormatSpec = %.0w
  FormatSpecOverTolerance = %+.0w
  FormatSpecUnderTolerance = %+.0w
  Inverted = false
  LineAngle = 0
  LockPosition = false
  MeasureType = 1
  OverTolerance = 0
  References2D = -> [ProjItem]
  Rotation = 0
  ScaleType = 0
  TheoreticalExact = false
  Type = 0
  UnderTolerance = 0
  X = -94.3387
  Y = 48.4174
FEATURE [TechDraw::DrawViewDimension] Dimension022
  AngleOverride = false
  Arbitrary = false
  ArbitraryTolerances = false
  EqualTolerance = true
  ExtensionAngle = 0
  FormatSpec = %.0w
  FormatSpecOverTolerance = %+.0w
  FormatSpecUnderTolerance = %+.0w
  Inverted = false
  LineAngle = 0
  LockPosition = false
  MeasureType = 1
  OverTolerance = 0
  References2D = -> [ProjItem]
  Rotation = 0
  ScaleType = 0
  TheoreticalExact = false
  Type = 0
  UnderTolerance = 0
  X = -89.2099
  Y = 35.68
FEATURE [TechDraw::DrawViewDimension] Dimension024
  AngleOverride = false
  Arbitrary = false
  ArbitraryTolerances = false
  EqualTolerance = true
  ExtensionAngle = 0
  FormatSpec = %.0w
  FormatSpecOverTolerance = %+.0w
  FormatSpecUnderTolerance = %+.0w
  Inverted = false
  LineAngle = 0
  LockPosition = false
  MeasureType = 1
  OverTolerance = 0
  References2D = -> [ProjItem]
  Rotation = 0
  ScaleType = 0
  TheoreticalExact = false
  Type = 7
  UnderTolerance = 0
  X = -45.6879
  Y = -12.7647
FEATURE [TechDraw::DrawViewDimension] Dimension025
  AngleOverride = false
  Arbitrary = false
  ArbitraryTolerances = false
  EqualTolerance = true
  ExtensionAngle = 0
  FormatSpec = %.0w
  FormatSpecOverTolerance = %+.0w
  FormatSpecUnderTolerance = %+.0w
  Inverted = false
  LineAngle = 0
  LockPosition = false
  MeasureType = 1
  OverTolerance = 0
  References2D = -> [ProjItem]
  Rotation = 0
  ScaleType = 0
  TheoreticalExact = false
  Type = 2
  UnderTolerance = 0
  X = -69.3174
  Y = 22.8232
FEATURE [TechDraw::DrawViewDimension] Dimension026
  AngleOverride = false
  Arbitrary = false
  ArbitraryTolerances = false
  EqualTolerance = true
  ExtensionAngle = 0
  FormatSpec = %.0w
  FormatSpecOverTolerance = %+.0w
  FormatSpecUnderTolerance = %+.0w
  Inverted = false
  LineAngle = 0
  LockPosition = false
  MeasureType = 1
  OverTolerance = 0
  References2D = -> [ProjItem]
  Rotation = 0
  ScaleType = 0
  TheoreticalExact = false
  Type = 1
  UnderTolerance = 0
  X = 1.32004
  Y = 10.4135
FEATURE [TechDraw::DrawPage] Page
  KeepUpdated = true
  NextBalloonIndex = 1
  ProjectionType = 0
  Template = -> Template
  Views = -> [ProjGroup,Dimension003,Dimension005,Dimension006,Dimension008,Dimension009,Dimension,Dimension010,Dimension016,Dimension020,Dimension021,Dimension022,Dimension024,Dimension025,Dimension026]
note: 1 file-system path scrubbed to <path> (originals preserved in the JSON sidecar)
